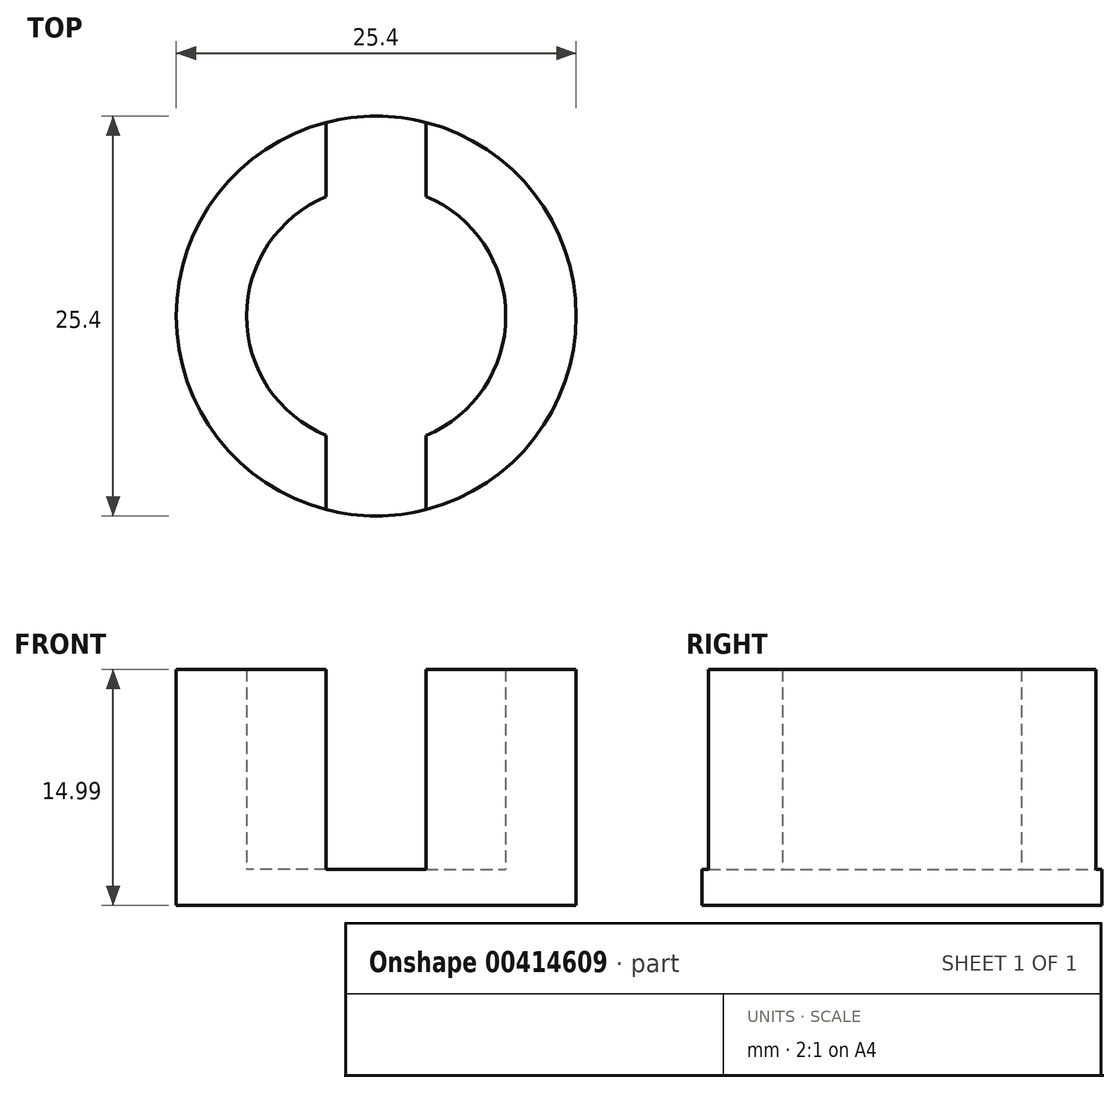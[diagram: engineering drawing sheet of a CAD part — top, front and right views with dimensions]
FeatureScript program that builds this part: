
annotation { "Feature Type Name" : "Feature", "Feature Type Description" : "" }
export const myFeature = defineFeature(function(context is Context, id is Id, definition is map)
    precondition{}
    {
        {
            var Q0;
            Q0=qCreatedBy(makeId("Top.planeOp"),FACE);
            var sketch = newSketch(context, id + "F0", { "sketchPlane" : qUnion([Q0])});
            skCircle(sketch, "E0", {"center": v(0, 0) * mm, "radius": 8.23 * mm});
            skCircle(sketch, "E1", {"center": v(0, 0) * mm, "radius": 12.7 * mm});
            skSolve(sketch);
        }
        {
            var Q0;
            Q0 = qSketchRegion(id + "F0", true);
            var Q1;
            Q1=makeQuery(id+"F0.imprint","IMPRINT",FACE,{"disambiguationData":[TD([[makeQuery(id+"F0.imprint","IMPRINT",EDGE,{"derivedFrom":sQuery(id+"F0.wireOp",EDGE,"E0")}),1.0]])]});
            extrude(context, id + "F1", {"entities" : qUnion([Q0, Q1]), "oppositeDirection" : true, "depth" : 2.3 * mm});
        }
        {
            var Q0;
            Q0 = qSketchRegion(id + "F0", true);
            extrude(context, id + "F2", {"entities" : qUnion([Q0]), "operationType" : NewBodyOperationType.ADD, "depth" : 12.7 * mm});
        }
        {
            var Q0;
            Q0=makeQuery(id+"F2.opExtrude","CAP_FACE",FACE,{"disambiguationData":[OSD([sQuery(id+"F0.wireOp",EDGE,"E0"),sQuery(id+"F0.wireOp",EDGE,"E1")])],"isStart":false});
            var sketch = newSketch(context, id + "F3", { "sketchPlane" : qUnion([Q0])});
            skLineSegment(sketch, "E2.bottom", {"start": v(3.18, 17.7) * mm, "end": v(-3.17, 17.7) * mm});
            skLineSegment(sketch, "E2.top", {"start": v(3.17, -17.7) * mm, "end": v(-3.18, -17.7) * mm});
            skLineSegment(sketch, "E2.left", {"start": v(3.18, 17.7) * mm, "end": v(3.17, -17.7) * mm});
            skLineSegment(sketch, "E2.right", {"start": v(-3.17, 17.7) * mm, "end": v(-3.18, -17.7) * mm});
            skPoint(sketch, "E2.middle", {"position": v(0, 0) * mm});
            skSolve(sketch);
        }
        {
            var Q0;
            Q0 = qSketchRegion(id + "F3", true);
            var Q1;
            Q1=makeQuery(id+"F1.opExtrude","CAP_FACE",FACE,{"disambiguationData":[OSD([sQuery(id+"F0.wireOp",EDGE,"E1")])],"isStart":true});
            extrude(context, id + "F4", {"entities" : qUnion([Q0]), "operationType" : NewBodyOperationType.REMOVE, "endBound" : BoundingType.UP_TO_SURFACE, "oppositeDirection" : true, "endBoundEntityFace" : qUnion([Q1]), "depth" : 25.4 * mm});
        }
    });
